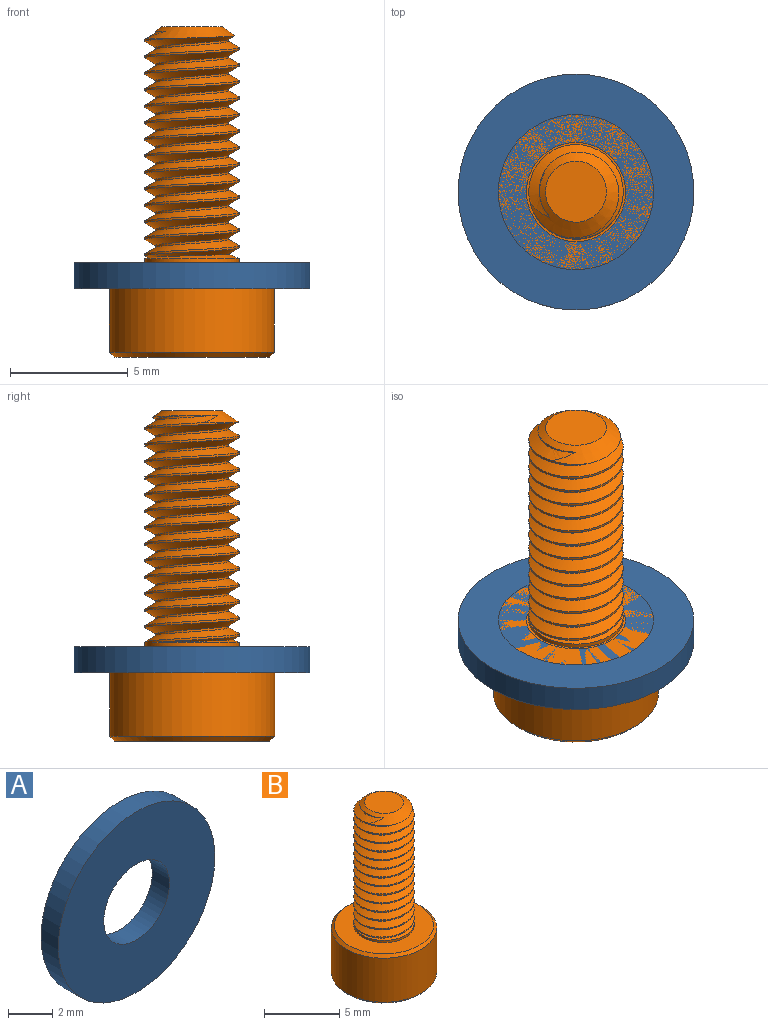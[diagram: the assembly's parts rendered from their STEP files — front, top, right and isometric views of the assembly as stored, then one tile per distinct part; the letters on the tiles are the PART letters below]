
ASSEMBLY  parts=2 mates=1
PART A: 4 faces, bbox 10x1.1x10 mm
  f0: cylinder r=2.1mm len=4.2mm, axis (0,1,0), area 14.5mm2, adj f2,f3
  f1: cylinder r=5mm len=10mm, axis (0,-1,0), area 34.6mm2, adj f2,f3
  f2: plane 10x10mm, normal (0,1,0), area 64.7mm2, adj f0,f1
  f3: plane 10x10mm, normal (0,-1,0), area 64.7mm2, adj f0,f1
PART B: 38 faces, bbox 7.7x7.7x14.7 mm
  f0: cone r=3.5mm half-angle=45deg, axis (0,0,-1), area 6.3mm2, adj f3,f24
  f1: cone r=3.29mm half-angle=45deg, axis (0,0,1), area 6.3mm2, adj f3,f23
  f2: cone r=1.73mm half-angle=45deg, axis (0,0,-1), area 0.3mm2, adj f23,f35
  f3: cylinder r=3.5mm len=7mm, axis (0,0,1), area 78.7mm2, adj f0,f1
  f4: cone r=1.29mm half-angle=55deg, axis (0,0,-1), area 5.8mm2, adj f5,f6,f20,f21,f22
  f5: cylinder r=1.55mm len=9.46mm, axis (0,0,-1), area 11.5mm2, adj f4,f20,f21,f37
  f6: cylinder r=2mm len=4mm, axis (0,0,1), area 0.7mm2, adj f4,f7,f20,f21
  f7: cylinder r=2mm len=4mm, axis (0,0,1), area 1.1mm2, adj f6,f8,f20,f21
  f8: cylinder r=2mm len=4mm, axis (0,0,1), area 1.1mm2, adj f7,f9,f20,f21
  f9: cylinder r=2mm len=4mm, axis (0,0,1), area 1.1mm2, adj f8,f10,f20,f21
  f10: cylinder r=2mm len=4mm, axis (0,0,1), area 1.1mm2, adj f9,f11,f20,f21
  f11: cylinder r=2mm len=4mm, axis (0,0,1), area 1.1mm2, adj f10,f12,f20,f21
  f12: cylinder r=2mm len=4mm, axis (0,0,1), area 1.1mm2, adj f11,f13,f20,f21
  f13: cylinder r=2mm len=4mm, axis (0,0,1), area 1.1mm2, adj f12,f14,f20,f21
  f14: cylinder r=2mm len=4mm, axis (0,0,1), area 1.1mm2, adj f13,f15,f20,f21
  f15: cylinder r=2mm len=4mm, axis (0,0,1), area 1.1mm2, adj f14,f16,f20,f21
  f16: cylinder r=2mm len=4mm, axis (0,0,1), area 1.1mm2, adj f15,f17,f20,f21
  f17: cylinder r=2mm len=4mm, axis (0,0,1), area 1.1mm2, adj f16,f18,f20,f21
  f18: cylinder r=2mm len=4mm, axis (0,0,1), area 1.1mm2, adj f17,f19,f20,f21
  f19: cylinder r=2mm len=4mm, axis (0,0,1), area 3mm2, adj f18,f20,f21,f24,f37
  f20: bspline ~10.17x4mm, area 78.6mm2, adj f4,f5,f6,f7,f8,f9,f10,f11
  f21: bspline ~9.83x4.62mm, area 78.6mm2, adj f4,f5,f6,f7,f8,f9,f10,f11
  f22: plane 2.58x2.58mm, normal (0,0,1), area 5.2mm2, adj f4
  f23: plane 7.15x7.15mm, normal (0,0,-1), area 24.6mm2, adj f1,f2,f25,f26,f27,f28,f29
  f24: plane 6.58x6.58mm, normal (0,0,1), area 21.4mm2, adj f0,f19
  f25: cone r=1.73mm half-angle=45deg, axis (0,0,-1), area 0mm2, adj f23,f31
  f26: cone r=1.73mm half-angle=45deg, axis (0,0,-1), area 0mm2, adj f23,f32
  f27: cone r=1.73mm half-angle=45deg, axis (0,0,-1), area 0mm2, adj f23,f33
  f28: cone r=1.73mm half-angle=45deg, axis (0,0,-1), area 0mm2, adj f23,f34
  f29: cone r=1.73mm half-angle=45deg, axis (0,0,-1), area 0mm2, adj f23,f36
  f30: plane 3.46x3mm, normal (0,0,-1), area 7.8mm2, adj f31,f32,f33,f34,f35,f36
  f31: plane 2.91x2.16mm, normal (-0.5,-0.87,0), area 3.6mm2, adj f25,f30,f32,f36
  f32: plane 2.91x2.39mm, normal (-1,0,0), area 3.6mm2, adj f26,f30,f31,f33
  f33: plane 2.91x2.16mm, normal (-0.5,0.87,0), area 3.6mm2, adj f27,f30,f32,f34
  f34: plane 2.91x2.16mm, normal (0.5,0.87,0), area 3.6mm2, adj f28,f30,f33,f35
  f35: plane 2.42x1.9mm, normal (1,0,0), area 3.6mm2, adj f2,f30,f34,f36
  f36: plane 2.91x2.16mm, normal (0.5,-0.87,0), area 3.6mm2, adj f29,f30,f31,f35
  f37: cone r=2mm half-angle=67.5deg, axis (0,0,-1), area 2.8mm2, adj f5,f19,f20,f21
PLACE A rot(axis=(-1,0,0),90deg) t=(0,-2,-9.54)mm
PLACE B t=(0,-2,0.46)mm
MATE fastened B.f0 <-> A.f0  axis (0,0,1) through (0,-2,-9.54)mm
